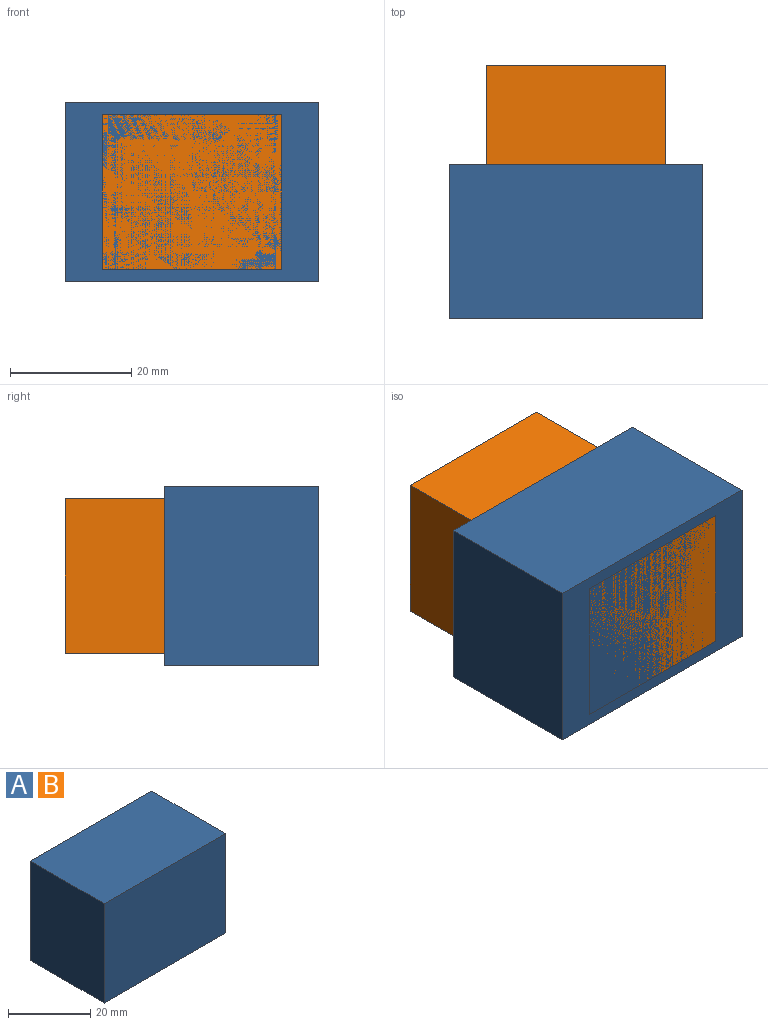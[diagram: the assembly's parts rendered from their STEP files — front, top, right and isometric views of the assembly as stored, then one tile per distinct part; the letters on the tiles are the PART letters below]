
ASSEMBLY  parts=2 mates=1
PART A: 6 faces, bbox 41.7x25.4x29.5 mm
  f0: plane 41.72x25.4mm, normal (0,0,1), area 1059.6mm2, adj f1,f3,f4,f5
  f1: plane 29.55x25.4mm, normal (-1,0,0), area 750.5mm2, adj f0,f2,f4,f5
  f2: plane 41.72x25.4mm, normal (0,0,-1), area 1059.6mm2, adj f1,f3,f4,f5
  f3: plane 29.55x25.4mm, normal (1,0,0), area 750.5mm2, adj f0,f2,f4,f5
  f4: plane 41.72x29.55mm, normal (0,-1,0), area 1232.6mm2, adj f0,f1,f2,f3
  f5: plane 41.72x29.55mm, normal (0,1,0), area 1232.6mm2, adj f0,f1,f2,f3
PART B: same geometry as A
PLACE A t=(47.87,32.2,-11.79)mm
PLACE B rot(axis=(-0.58,0.58,-0.58),120deg) t=(9.36,6.8,-6.84)mm
MATE revolute B.f3 <-> A.f4  axis (0,-1,0) through (27.01,6.8,5.86)mm
